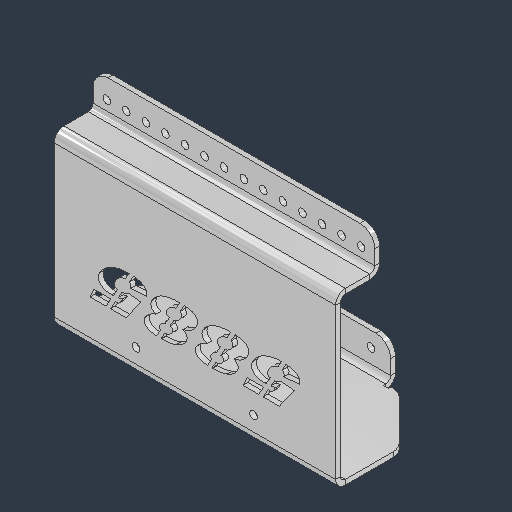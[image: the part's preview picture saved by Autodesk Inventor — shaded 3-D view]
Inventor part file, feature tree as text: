
AUTODESK INVENTOR PART (.ipt)
format: ipt  version: 2024.3 (Build 283343000, 343)  size: 866,816 bytes
history: native  units: in
note: dims shown in document units (in); Inventor stores cm internally (conversion verified against a paired STEP export)
features: sheet_metal_op x13, sketch x9, other x7, hole x2, extrude x2, pattern_linear x1, chamfer x1, projected_geometry x1
ambient origin geometry x8: Origin, YZ Plane, XZ Plane, XY Plane, X Axis, Y Axis, Z Axis, Center Point
bodies: Solid1 (feature_tree)
feature tree (36):
  sheet_metal_op  "Face1"
  sheet_metal_op  "Flange3"
  sheet_metal_op  "Flange4"
  hole  "Hole3"  [1 undecoded]
  sheet_metal_op  "Flange5"
  sheet_metal_op  "Flange6"
  hole  "Hole4"  [1 undecoded]
  pattern_linear  "Rectangular Pattern1"  Count1=4 Spacing1=1.3in
  other  "Corner Chamfer2"
  chamfer  "Corner Round1"
  extrude  "Extrusion1"  Depth=1.25in
  extrude  "Extrusion2"  Depth=0.1in
  sketch  "Sketch1"  dims[d0=7.1875in d1=4.1in]
  other  "Plate1"
  sketch  "Sketch6"  dims[d2=0.125in d51=0.375in]
  sketch  "Sketch7"  dims[d57=0.0in d58=0.0in d59=1.5748in d61=1.3in d62=0.3937in d64=1.0in]
  sketch  "Sketch8"  dims[d67=0.375in d68=1.25in]
  other  "Plate4"
  sheet_metal_op  "Bend3"
  sheet_metal_op  "Corner3"
  sketch  "Sketch9"  dims[d69=0.1in d70=0.2in]
  other  "Plate5"
  sheet_metal_op  "Bend4"
  sheet_metal_op  "Corner4"
  sketch  "Sketch10"  dims[d71=60.0deg]
  projected_geometry  "Projected Loop1"
  sketch  "Sketch11"  dims[d72=1.0in d73=0.0in]
  other  "Plate6"
  sheet_metal_op  "Bend5"
  sheet_metal_op  "Corner5"
  sketch  "Sketch12"  dims[d74=3.2188in]
  other  "Plate7"
  sheet_metal_op  "Bend6"
  sheet_metal_op  "Corner6"
  sketch  "Sketch13"  dims[d75=2.8438in d76=1.0in d77=0.125in d78=0.0625in d79=0.25in d80=0.125in d81=2.875in d82=90.0deg d83=0.125in d84=0.5in d85=0.125in d86=0.125in d87=0.125in d88=0.0625in d89=0.25in d90=0.125in d91=1.0in d92=90.0deg d93=0.125in d94=0.5in d95=0.125in d96=0.125in d98=0.5in d99=3.0in d100=0.201in d101=0.75in d102=0.375in d103=0.25in d104=0.5635in d105=1.0in d106=0.8108in d107=4.0in d108=1.25in d109=0.25in d110=60.0deg d111=0.125in d112=0.0625in d113=0.25in d114=0.125in d115=1.125in d116=90.0deg d117=0.125in d118=0.5in d119=0.125in d120=0.125in d121=0.125in d122=0.0625in d123=0.25in d124=0.125in d125=1.0in d126=90.0deg d127=0.125in d128=0.5in d129=0.125in d130=0.125in d131=0.5in d132=0.196in d133=0.75in d134=0.385in d135=0.077in d136=0.5635in d137=0.125in d138=0.8108in d139=0.5in d140=2.7559in d142=1.0in]
  other  "Definition1"
note: 2 required parameter values undecoded (feature->parameter linkage not recoverable at this tier; creation-order binding heuristic only, values carry confidence <= 0.55)
